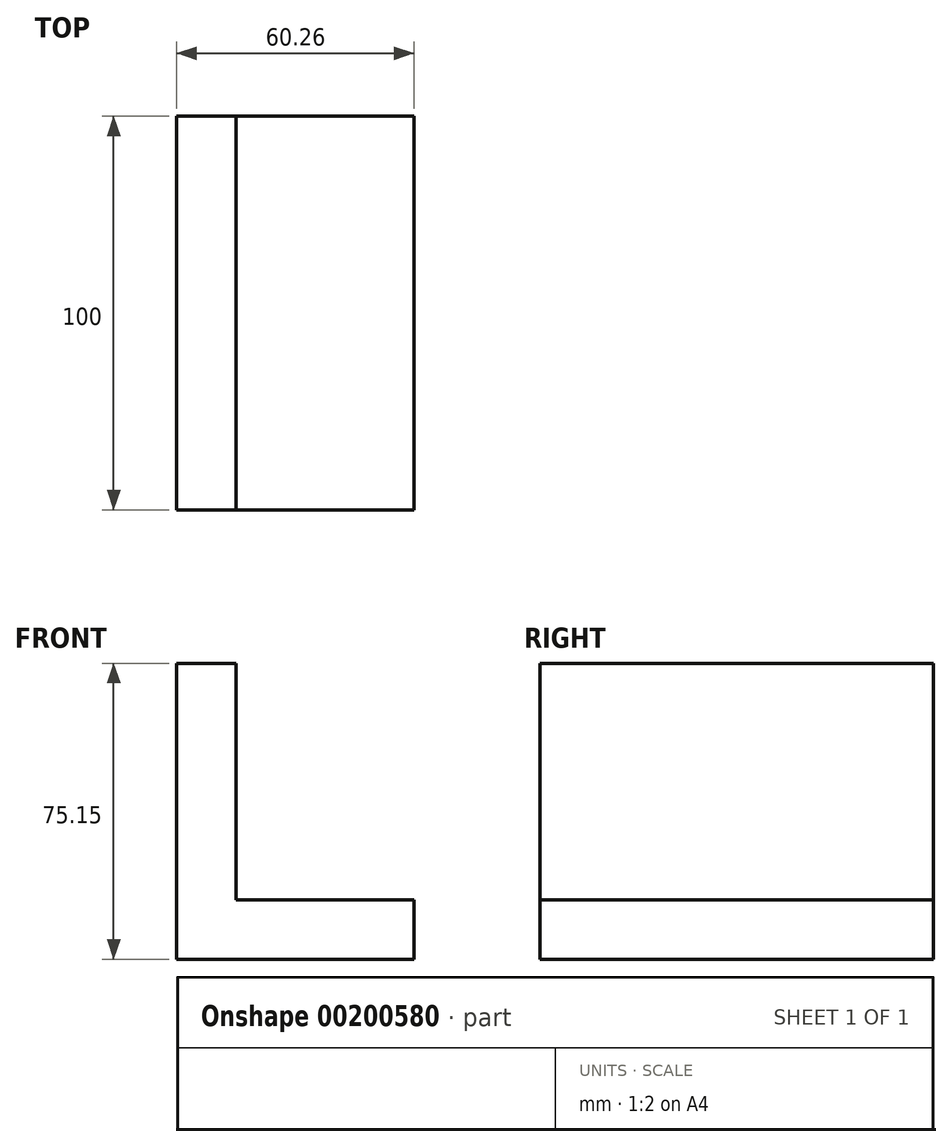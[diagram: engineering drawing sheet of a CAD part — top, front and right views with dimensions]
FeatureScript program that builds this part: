
annotation { "Feature Type Name" : "Feature", "Feature Type Description" : "" }
export const myFeature = defineFeature(function(context is Context, id is Id, definition is map)
    precondition{}
    {
        {
            var Q0;
            Q0=qCreatedBy(makeId("Front.planeOp"),FACE);
            var sketch = newSketch(context, id + "F0", { "sketchPlane" : qUnion([Q0])});
            skLineSegment(sketch, "E0", {"start": v(39.12, -16.82) * mm, "end": v(-21.14, -16.82) * mm});
            skLineSegment(sketch, "E1", {"start": v(-21.14, -16.82) * mm, "end": v(-21.14, 58.33) * mm});
            skLineSegment(sketch, "E2", {"start": v(-21.14, 58.33) * mm, "end": v(-6.02, 58.33) * mm});
            skLineSegment(sketch, "E3", {"start": v(-6.02, 58.33) * mm, "end": v(-6.02, -1.7) * mm});
            skLineSegment(sketch, "E4", {"start": v(-6.02, -1.7) * mm, "end": v(39.12, -1.7) * mm});
            skLineSegment(sketch, "E5", {"start": v(39.12, -1.7) * mm, "end": v(39.12, -16.82) * mm});
            skSolve(sketch);
        }
        {
            var Q0;
            Q0=makeQuery(id+"F0.imprint","IMPRINT",FACE,{"disambiguationData":[TD([[makeQuery(id+"F0.imprint","IMPRINT",EDGE,{"derivedFrom":sQuery(id+"F0.wireOp",EDGE,"E0")}),-1.0]])]});
            extrude(context, id + "F1", {"entities" : qUnion([Q0]), "depth" : 100 * mm});
        }
    });
